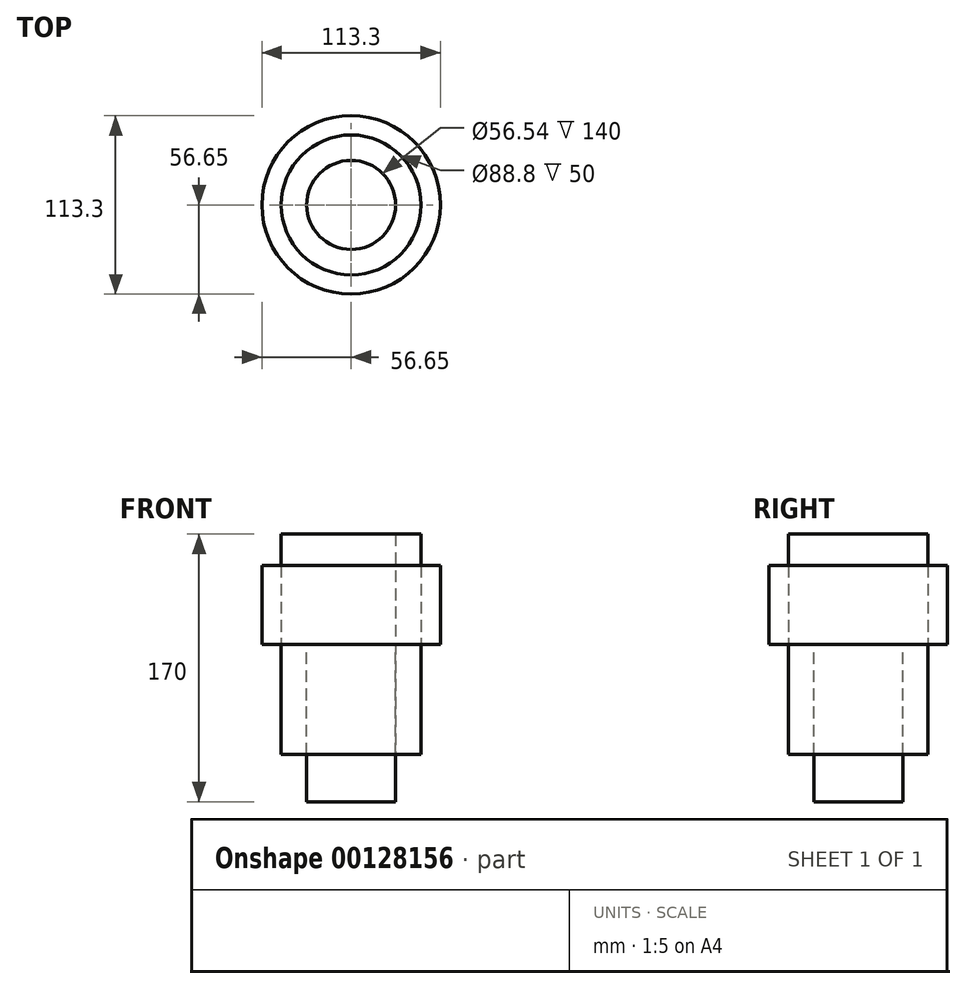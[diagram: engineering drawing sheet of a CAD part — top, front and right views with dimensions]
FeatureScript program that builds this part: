
annotation { "Feature Type Name" : "Feature", "Feature Type Description" : "" }
export const myFeature = defineFeature(function(context is Context, id is Id, definition is map)
    precondition{}
    {
        {
            var Q0;
            Q0=qCreatedBy(makeId("Top.planeOp"),FACE);
            var sketch = newSketch(context, id + "F0", { "sketchPlane" : qUnion([Q0])});
            skCircle(sketch, "E0", {"center": v(0, 0) * mm, "radius": 56.65 * mm});
            skCircle(sketch, "E1", {"center": v(0, 0) * mm, "radius": 28.27 * mm});
            skCircle(sketch, "E2", {"center": v(0, 0) * mm, "radius": 44.4 * mm});
            skSolve(sketch);
        }
        {
            var Q0;
            Q0=makeQuery(id+"F0.imprint","IMPRINT",FACE,{"disambiguationData":[TD([[makeQuery(id+"F0.imprint","IMPRINT",EDGE,{"derivedFrom":sQuery(id+"F0.wireOp",EDGE,"E0")}),1.0]])]});
            extrude(context, id + "F1", {"entities" : qUnion([Q0]), "depth" : 50 * mm});
        }
        {
            var Q0;
            Q0=makeQuery(id+"F0.imprint","IMPRINT",FACE,{"disambiguationData":[TD([[makeQuery(id+"F0.imprint","IMPRINT",EDGE,{"derivedFrom":sQuery(id+"F0.wireOp",EDGE,"E1")}),1.0]])]});
            extrude(context, id + "F2", {"entities" : qUnion([Q0]), "oppositeDirection" : true, "depth" : 100 * mm});
        }
        {
            var Q0;
            Q0=makeQuery(id+"F0.imprint","IMPRINT",FACE,{"disambiguationData":[TD([[makeQuery(id+"F0.imprint","IMPRINT",EDGE,{"derivedFrom":sQuery(id+"F0.wireOp",EDGE,"E1")}),-1.0]])]});
            extrude(context, id + "F3", {"entities" : qUnion([Q0]), "depth" : 70 * mm, "hasSecondDirection" : true, "secondDirectionOppositeDirection" : true, "secondDirectionDepth" : 70 * mm});
        }
    });
